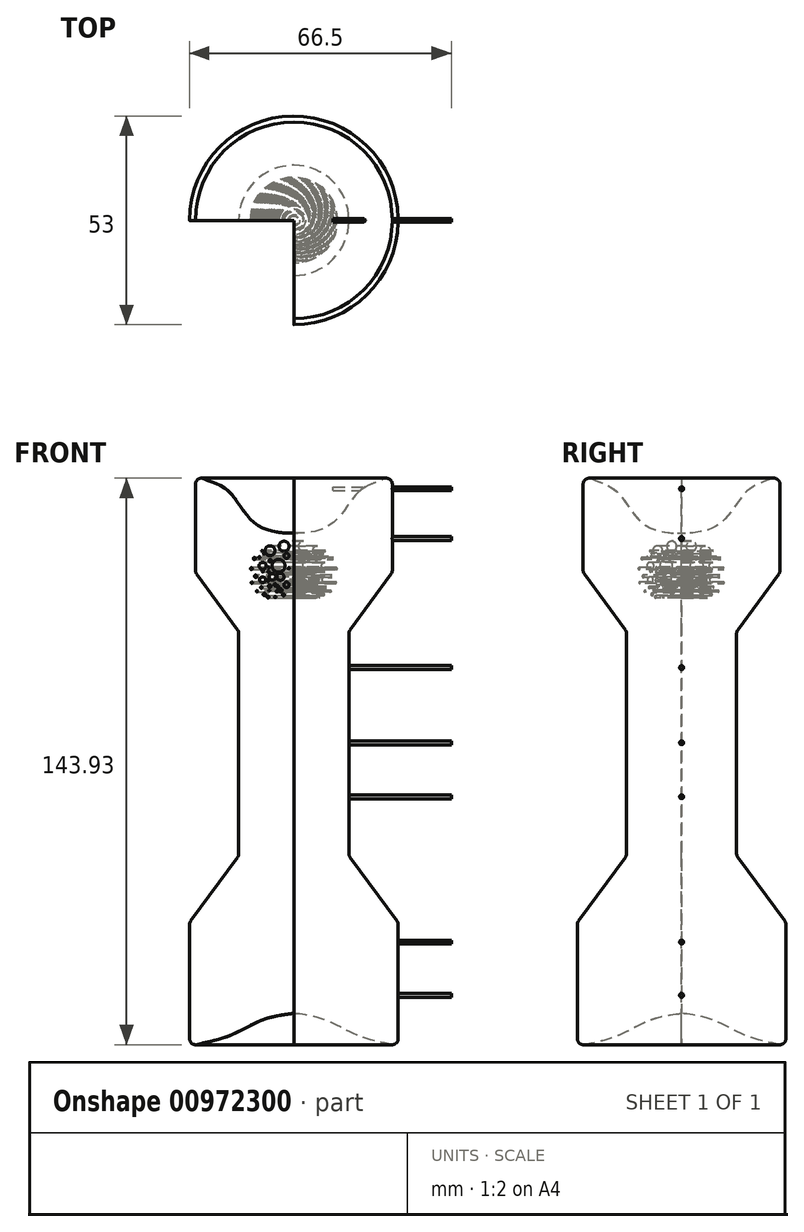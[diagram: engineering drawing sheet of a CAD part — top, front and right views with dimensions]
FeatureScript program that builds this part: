
annotation { "Feature Type Name" : "Feature", "Feature Type Description" : "" }
export const myFeature = defineFeature(function(context is Context, id is Id, definition is map)
    precondition{}
    {
        {
            var Q0;
            Q0=qCreatedBy(makeId("Front.planeOp"),FACE);
            var sketch = newSketch(context, id + "F0", { "sketchPlane" : qUnion([Q0])});
            skLineSegment(sketch, "E0", {"start": v(-26.5, 1.5) * mm, "end": v(-26.5, 30.5) * mm});
            skLineSegment(sketch, "E1", {"start": v(-26.2, 31.4) * mm, "end": v(-14.3, 47.6) * mm});
            skLineSegment(sketch, "E2", {"start": v(-14, 48.5) * mm, "end": v(-14, 104.5) * mm});
            skLineSegment(sketch, "E3", {"start": v(-14.3, 105.4) * mm, "end": v(-24.7, 119.6) * mm});
            skLineSegment(sketch, "E4", {"start": v(-25, 120.5) * mm, "end": v(-25, 142.43) * mm});
            skLineSegment(sketch, "E5", {"start": v(0, 130) * mm, "end": v(0, 7.98) * mm});
            skPoint(sketch, "E6.visualSharp", {"position": v(-25, 77.77) * mm});
            skFitSpline(sketch, "E7", {"points": [v(-25, 145) * mm, v(-16.99, 140.94) * mm, v(-9.43, 132.13) * mm, v(0, 130) * mm], "startDerivative": vector(20.03, -15.94) * mm, "endDerivative": vector(20.73, 1.21) * mm});
            skArc(sketch, "E8.filletArc", {"start": v(-22.9, 143.8) * mm, "mid": v(-24.32, 143.68) * mm, "end": v(-25, 142.43) * mm});
            skPoint(sketch, "E9.visualSharp", {"position": v(-25, 120) * mm});
            skArc(sketch, "E9.filletArc", {"start": v(-25, 120.5) * mm, "mid": v(-24.93, 120.02) * mm, "end": v(-24.7, 119.6) * mm});
            skPoint(sketch, "E10.visualSharp", {"position": v(-14, 105) * mm});
            skArc(sketch, "E10.filletArc", {"start": v(-14, 104.5) * mm, "mid": v(-14.07, 104.98) * mm, "end": v(-14.3, 105.4) * mm});
            skPoint(sketch, "E11.visualSharp", {"position": v(-14, 48) * mm});
            skArc(sketch, "E11.filletArc", {"start": v(-14.3, 47.6) * mm, "mid": v(-14.07, 48.02) * mm, "end": v(-14, 48.5) * mm});
            skPoint(sketch, "E12.visualSharp", {"position": v(-26.5, 31) * mm});
            skArc(sketch, "E12.filletArc", {"start": v(-26.2, 31.4) * mm, "mid": v(-26.43, 30.98) * mm, "end": v(-26.5, 30.5) * mm});
            skPoint(sketch, "E13.visualSharp", {"position": v(-26.5, 0) * mm});
            skArc(sketch, "E13.filletArc", {"start": v(-26.5, 1.5) * mm, "mid": v(-26.06, 0.44) * mm, "end": v(-25, 0) * mm});
            skFitSpline(sketch, "E14", {"points": [v(-25, 0) * mm, v(-15.8, 2.5) * mm, v(-8.07, 6.26) * mm, v(0, 7.98) * mm], "startDerivative": vector(27.44, 5.64) * mm, "endDerivative": vector(25.58, 3.45) * mm});
            skSolve(sketch);
        }
        {
            var Q0;
            Q0=qSketchRegion(id+"F0",true);
            var Q1;
            Q1=sQuery(id+"F0.wireOp",EDGE,"E5");
            revolve(context, id + "F1", {"entities" : qUnion([Q0]), "axis" : qUnion([Q1]), "revolveType" : RevolveType.ONE_DIRECTION, "angle" : 270 * degree});
        }
        {
            var Q0;
            Q0=qCreatedBy(makeId("Right.planeOp"),FACE);
            var sketch = newSketch(context, id + "F2", { "sketchPlane" : qUnion([Q0])});
            skCircle(sketch, "E15", {"center": v(-2.5, 126.64) * mm, "radius": 1.27 * mm});
            skCircle(sketch, "E16", {"center": v(-6.07, 125.5) * mm, "radius": 1.26 * mm});
            skCircle(sketch, "E17", {"center": v(-3.9, 121.67) * mm, "radius": 1.63 * mm});
            skCircle(sketch, "E18", {"center": v(-7.94, 121.67) * mm, "radius": 0.89 * mm});
            skCircle(sketch, "E19", {"center": v(-7.94, 118.1) * mm, "radius": 0.74 * mm});
            skCircle(sketch, "E20", {"center": v(-3.4, 118.86) * mm, "radius": 0.9 * mm});
            skCircle(sketch, "E21", {"center": v(-5.43, 118.86) * mm, "radius": 0.85 * mm});
            skCircle(sketch, "E22", {"center": v(-1.86, 116.82) * mm, "radius": 0.69 * mm});
            skCircle(sketch, "E23", {"center": v(-1.86, 124.22) * mm, "radius": 0.65 * mm});
            skCircle(sketch, "E24", {"center": v(-4.14, 116.45) * mm, "radius": 0.28 * mm});
            skCircle(sketch, "E25", {"center": v(-4.8, 116.88) * mm, "radius": 0.28 * mm});
            skCircle(sketch, "E26", {"center": v(-3.33, 115.46) * mm, "radius": 0.4 * mm});
            skCircle(sketch, "E27", {"center": v(-1.3, 121.03) * mm, "radius": 0.17 * mm});
            skCircle(sketch, "E28", {"center": v(-5.96, 122.93) * mm, "radius": 0.35 * mm});
            skCircle(sketch, "E29", {"center": v(-8.75, 123.79) * mm, "radius": 0.2 * mm});
            skCircle(sketch, "E30", {"center": v(-10.78, 120.92) * mm, "radius": 0.25 * mm});
            skCircle(sketch, "E31", {"center": v(-7.89, 120.36) * mm, "radius": 0.25 * mm});
            skCircle(sketch, "E32", {"center": v(-6.39, 121.19) * mm, "radius": 0.19 * mm});
            skCircle(sketch, "E33", {"center": v(-6.44, 120.12) * mm, "radius": 0.19 * mm});
            skCircle(sketch, "E34", {"center": v(-6.55, 117.92) * mm, "radius": 0.22 * mm});
            skCircle(sketch, "E35", {"center": v(-6.15, 116.5) * mm, "radius": 0.34 * mm});
            skCircle(sketch, "E36", {"center": v(-8.26, 116.15) * mm, "radius": 0.2 * mm});
            skCircle(sketch, "E37", {"center": v(-6.25, 115.43) * mm, "radius": 0.15 * mm});
            skCircle(sketch, "E38", {"center": v(-4.27, 115.21) * mm, "radius": 0.2 * mm});
            skCircle(sketch, "E39", {"center": v(-2.61, 114.28) * mm, "radius": 0.27 * mm});
            skCircle(sketch, "E40", {"center": v(-4.73, 113.71) * mm, "radius": 0.16 * mm});
            skCircle(sketch, "E41", {"center": v(-6.6, 113.77) * mm, "radius": 0.26 * mm});
            skCircle(sketch, "E42", {"center": v(-7.49, 114.38) * mm, "radius": 0.31 * mm});
            skCircle(sketch, "E43", {"center": v(-9.39, 115.19) * mm, "radius": 0.16 * mm});
            skCircle(sketch, "E44", {"center": v(-10.68, 117.39) * mm, "radius": 0.17 * mm});
            skCircle(sketch, "E45", {"center": v(-9.71, 119) * mm, "radius": 0.3 * mm});
            skCircle(sketch, "E46", {"center": v(-10.03, 123.5) * mm, "radius": 0.28 * mm});
            skCircle(sketch, "E47", {"center": v(-8.08, 125.47) * mm, "radius": 0.13 * mm});
            skCircle(sketch, "E48", {"center": v(-7.6, 124.77) * mm, "radius": 0.15 * mm});
            skSolve(sketch);
        }
        {
            var Q0;
            Q0=qSketchRegion(id+"F2",true);
            var Q1;
            Q1=makeQuery(id+"F1.opRevolve","CAP_EDGE",EDGE,{"disambiguationData":[OSD([sQuery(id+"F0.wireOp",EDGE,"E5")])],"isStart":true});
            revolve(context, id + "F3", {"operationType" : NewBodyOperationType.REMOVE, "entities" : qUnion([Q0]), "axis" : qUnion([Q1]), "revolveType" : RevolveType.FULL, "oppositeDirection" : true});
        }
        {
            var Q0;
            Q0=qCreatedBy(makeId("Right.planeOp"),FACE);
            cPlane(context, id + "F4", {"entities" : qUnion([Q0]), "cplaneType" : CPlaneType.OFFSET, "offset" : 40 * mm, "width" : 150 * mm, "height" : 150 * mm});
        }
        {
            var Q0;
            Q0=qCreatedBy(id+"F4.planeOp",FACE);
            var sketch = newSketch(context, id + "F5", { "sketchPlane" : qUnion([Q0])});
            skCircle(sketch, "E49", {"center": v(0, 12.54) * mm, "radius": 0.5 * mm});
            skCircle(sketch, "E50", {"center": v(0, 63) * mm, "radius": 0.5 * mm});
            skCircle(sketch, "E51", {"center": v(0, 76.71) * mm, "radius": 0.5 * mm});
            skCircle(sketch, "E52", {"center": v(0, 95.8) * mm, "radius": 0.5 * mm});
            skCircle(sketch, "E53", {"center": v(0, 128.59) * mm, "radius": 0.5 * mm});
            skCircle(sketch, "E54", {"center": v(0, 141.24) * mm, "radius": 0.5 * mm});
            skCircle(sketch, "E55", {"center": v(0, 26.06) * mm, "radius": 0.5 * mm});
            skSolve(sketch);
        }
        {
            var Q0;
            Q0=qSketchRegion(id+"F5",true);
            extrude(context, id + "F6", {"entities" : qUnion([Q0]), "operationType" : NewBodyOperationType.ADD, "oppositeDirection" : true, "depth" : 30 * mm});
        }
    });
